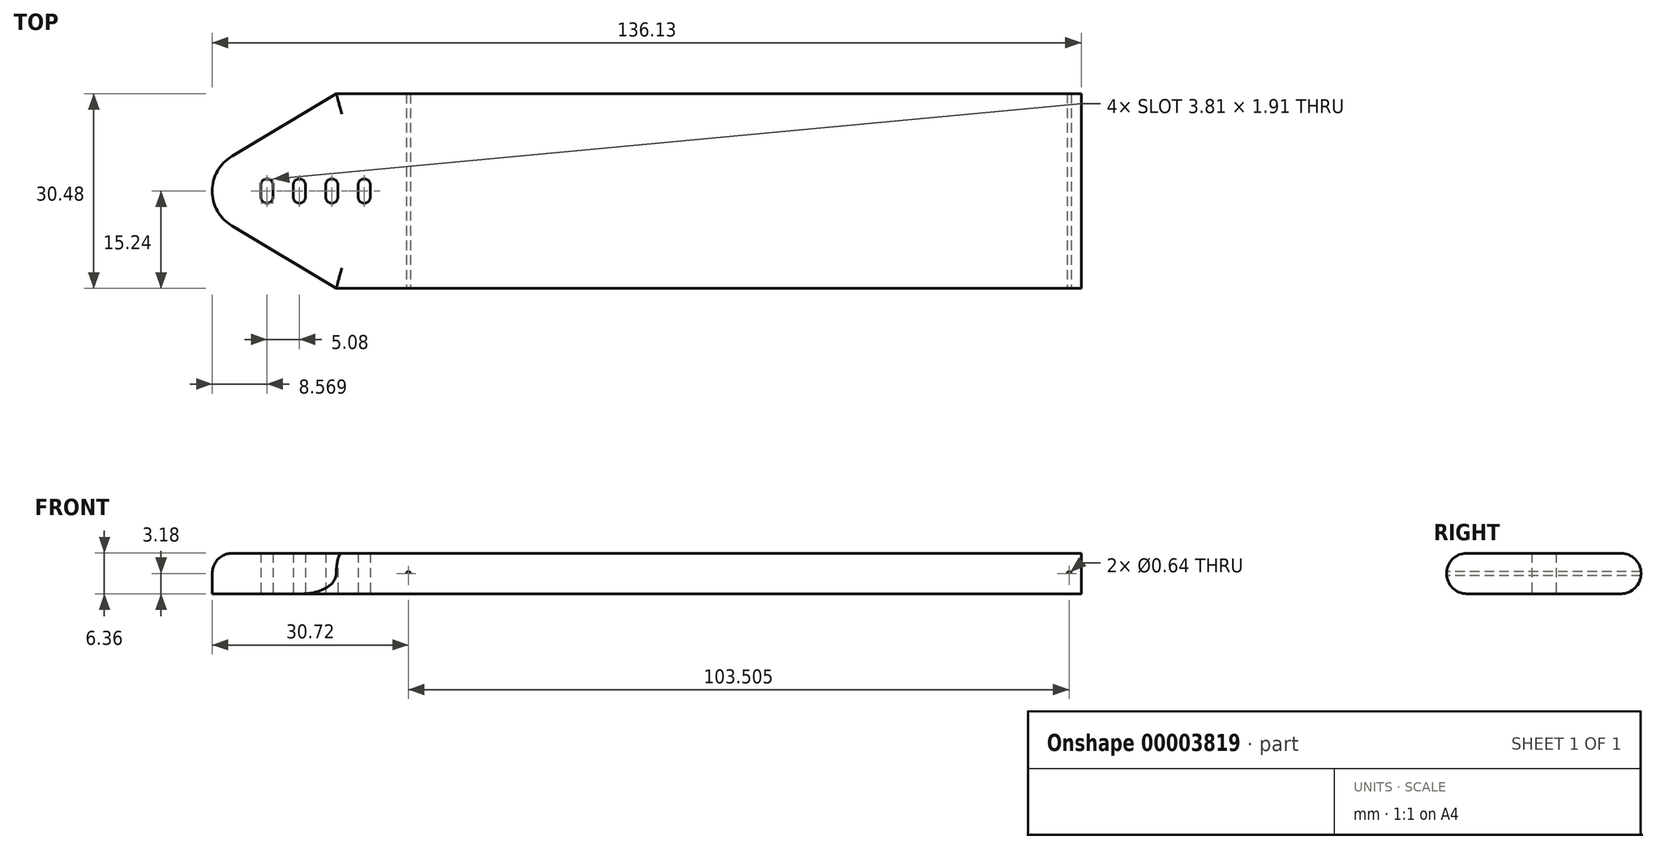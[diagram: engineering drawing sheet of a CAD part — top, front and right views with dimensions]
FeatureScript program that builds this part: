
annotation { "Feature Type Name" : "Feature", "Feature Type Description" : "" }
export const myFeature = defineFeature(function(context is Context, id is Id, definition is map)
    precondition{}
    {
        {
            var Q0;
            Q0=qCreatedBy(makeId("Right.planeOp"),FACE);
            var sketch = newSketch(context, id + "F0", { "sketchPlane" : qUnion([Q0])});
            skLineSegment(sketch, "E0.rect.bottom", {"start": v(15.24, -3.17) * mm, "end": v(-15.24, -3.18) * mm});
            skLineSegment(sketch, "E0.rect.top", {"start": v(15.24, 3.18) * mm, "end": v(-15.24, 3.18) * mm});
            skLineSegment(sketch, "E0.rect.left", {"start": v(15.24, -3.17) * mm, "end": v(15.24, 3.18) * mm});
            skLineSegment(sketch, "E0.rect.right", {"start": v(-15.24, -3.17) * mm, "end": v(-15.24, 3.18) * mm});
            skPoint(sketch, "E0.rect.middle", {"position": v(0, 0) * mm});
            skSolve(sketch);
        }
        {
            var Q0;
            Q0=qCreatedBy(makeId("Front.planeOp"),FACE);
            var sketch = newSketch(context, id + "F1", { "sketchPlane" : qUnion([Q0])});
            skLineSegment(sketch, "E1", {"start": v(0, 0) * mm, "end": v(95.25, 0) * mm});
            skPoint(sketch, "E2.end.orphan", {"position": v(0, 50.8) * mm});
            skSolve(sketch);
        }
        {
            var Q0;
            Q0=makeQuery(id+"F0.imprint","IMPRINT",FACE,{"disambiguationData":[TD([[makeQuery(id+"F0.imprint","IMPRINT",EDGE,{"derivedFrom":sQuery(id+"F0.wireOp",EDGE,"E0.rect.bottom")}),-1.0]])]});
            var Q1;
            Q1=sQuery(id+"F1.wireOp",EDGE,"E1");
            sweep(context, id + "F2", {"profiles" : qUnion([Q0]), "path" : qUnion([Q1])});
        }
        {
            var Q0;
            Q0=makeQuery(id+"F2.opSweep","CAP_FACE",FACE,{"disambiguationData":[OSD([sQuery(id+"F0.wireOp",EDGE,"E0.rect.bottom"),sQuery(id+"F0.wireOp",EDGE,"E0.rect.top"),sQuery(id+"F0.wireOp",EDGE,"E0.rect.left"),sQuery(id+"F0.wireOp",EDGE,"E0.rect.right"),sQuery(id+"F1.wireOp",VERTEX,"E1.end")])],"isStart":false});
            var sketch = newSketch(context, id + "F3", { "sketchPlane" : qUnion([Q0])});
            skLineSegment(sketch, "E3.bottom", {"start": v(15.24, 3.17) * mm, "end": v(-15.24, 3.17) * mm});
            skLineSegment(sketch, "E3.top", {"start": v(15.24, -3.17) * mm, "end": v(-15.24, -3.18) * mm});
            skLineSegment(sketch, "E3.left", {"start": v(-15.24, -3.18) * mm, "end": v(-15.24, 3.17) * mm});
            skLineSegment(sketch, "E3.right", {"start": v(15.24, -3.18) * mm, "end": v(15.24, 3.17) * mm});
            skSolve(sketch);
        }
        {
            var Q0;
            Q0=makeQuery(id+"F3.imprint","IMPRINT",FACE,{"disambiguationData":[TD([[makeQuery(id+"F3.imprint","IMPRINT",EDGE,{"derivedFrom":sQuery(id+"F3.wireOp",EDGE,"E3.bottom")}),1.0]])]});
            extrude(context, id + "F4", {"entities" : qUnion([Q0]), "operationType" : NewBodyOperationType.ADD, "depth" : 12.7 * mm});
        }
        {
            var Q0;
            Q0=makeQuery(id+"F4.boolean.opBoolean","MERGE",FACE,{"derivedFrom":[makeQuery(id+"F2.opSweep","SWEPT_FACE",FACE,{"disambiguationData":[OSD([sQuery(id+"F0.wireOp",EDGE,"E0.rect.right"),sQuery(id+"F1.wireOp",EDGE,"E1")])]}),makeQuery(id+"F4.opExtrude","SWEPT_FACE",FACE,{"disambiguationData":[OSD([sQuery(id+"F3.wireOp",EDGE,"E3.left")])]})]});
            var sketch = newSketch(context, id + "F5", { "sketchPlane" : qUnion([Q0])});
            skCircle(sketch, "E4", {"center": v(2.54, 0) * mm, "radius": 0.32 * mm});
            skSolve(sketch);
        }
        {
            var Q0;
            Q0=makeQuery(id+"F5.imprint","IMPRINT",FACE,{"disambiguationData":[TD([[makeQuery(id+"F5.imprint","IMPRINT",EDGE,{"derivedFrom":sQuery(id+"F5.wireOp",EDGE,"E4")}),1.0]])]});
            extrude(context, id + "F6", {"entities" : qUnion([Q0]), "operationType" : NewBodyOperationType.REMOVE, "endBound" : BoundingType.THROUGH_ALL, "oppositeDirection" : true, "depth" : 25.4 * mm});
        }
        {
            var Q0;
            Q0=makeQuery(id+"F4.boolean.opBoolean","MERGE",FACE,{"derivedFrom":[makeQuery(id+"F2.opSweep","SWEPT_FACE",FACE,{"disambiguationData":[OSD([sQuery(id+"F0.wireOp",EDGE,"E0.rect.right"),sQuery(id+"F1.wireOp",EDGE,"E1")])]}),makeQuery(id+"F4.opExtrude","SWEPT_FACE",FACE,{"disambiguationData":[OSD([sQuery(id+"F3.wireOp",EDGE,"E3.left")])]})]});
            var sketch = newSketch(context, id + "F7", { "sketchPlane" : qUnion([Q0])});
            skCircle(sketch, "E5", {"center": v(106.05, 0) * mm, "radius": 0.32 * mm});
            skLineSegment(sketch, "E6", {"start": v(107.95, 0) * mm, "end": v(114.08, 0) * mm, "construction": true});
            skSolve(sketch);
        }
        {
            var Q0;
            Q0=makeQuery(id+"F7.imprint","IMPRINT",FACE,{"disambiguationData":[TD([[makeQuery(id+"F7.imprint","IMPRINT",EDGE,{"derivedFrom":sQuery(id+"F7.wireOp",EDGE,"E5")}),1.0]])]});
            extrude(context, id + "F8", {"entities" : qUnion([Q0]), "operationType" : NewBodyOperationType.REMOVE, "endBound" : BoundingType.THROUGH_ALL, "oppositeDirection" : true, "depth" : 25.4 * mm});
        }
        {
            var Q0;
            Q0=makeQuery(id+"F2.opSweep","CAP_FACE",FACE,{"disambiguationData":[OSD([sQuery(id+"F0.wireOp",EDGE,"E0.rect.bottom"),sQuery(id+"F0.wireOp",EDGE,"E0.rect.top"),sQuery(id+"F0.wireOp",EDGE,"E0.rect.left"),sQuery(id+"F0.wireOp",EDGE,"E0.rect.right"),sQuery(id+"F1.wireOp",VERTEX,"E1.start")])],"isStart":true});
            var sketch = newSketch(context, id + "F9", { "sketchPlane" : qUnion([Q0])});
            skLineSegment(sketch, "E7.bottom", {"start": v(15.24, -3.18) * mm, "end": v(-15.24, -3.18) * mm});
            skLineSegment(sketch, "E7.top", {"start": v(15.24, 3.18) * mm, "end": v(-15.24, 3.18) * mm});
            skLineSegment(sketch, "E7.left", {"start": v(15.24, -3.18) * mm, "end": v(15.24, 3.18) * mm});
            skLineSegment(sketch, "E7.right", {"start": v(-15.24, -3.18) * mm, "end": v(-15.24, 3.18) * mm});
            skSolve(sketch);
        }
        {
            var Q0;
            Q0=makeQuery(id+"F9.imprint","IMPRINT",FACE,{"disambiguationData":[TD([[makeQuery(id+"F9.imprint","IMPRINT",EDGE,{"derivedFrom":sQuery(id+"F9.wireOp",EDGE,"E7.bottom")}),-1.0]])]});
            extrude(context, id + "F10", {"entities" : qUnion([Q0]), "operationType" : NewBodyOperationType.ADD, "depth" : 31.75 * mm});
        }
        {
            var Q0;
            Q0=makeQuery(id+"F10.boolean.opBoolean","MERGE",FACE,{"derivedFrom":[makeQuery(id+"F4.boolean.opBoolean","MERGE",FACE,{"derivedFrom":[makeQuery(id+"F2.opSweep","SWEPT_FACE",FACE,{"disambiguationData":[OSD([sQuery(id+"F0.wireOp",EDGE,"E0.rect.bottom"),sQuery(id+"F1.wireOp",EDGE,"E1")])]}),makeQuery(id+"F4.opExtrude","SWEPT_FACE",FACE,{"disambiguationData":[OSD([sQuery(id+"F3.wireOp",EDGE,"E3.top")])]})]}),makeQuery(id+"F10.opExtrude","SWEPT_FACE",FACE,{"disambiguationData":[OSD([sQuery(id+"F9.wireOp",EDGE,"E7.bottom")])]})]});
            var sketch = newSketch(context, id + "F11", { "sketchPlane" : qUnion([Q0])});
            skLineSegment(sketch, "E8", {"start": v(0, 0) * mm, "end": v(-31.75, 0) * mm, "construction": true});
            skLineSegment(sketch, "E9", {"start": v(-25.1, 5.45) * mm, "end": v(-8.76, 15.24) * mm});
            skLineSegment(sketch, "E10.0.MirrorCS", {"start": v(-25.1, -5.45) * mm, "end": v(-8.76, -15.24) * mm});
            skPoint(sketch, "E11.start.orphan", {"position": v(-34.19, 0) * mm});
            skArc(sketch, "E12.filletArc", {"start": v(-25.1, 5.45) * mm, "mid": v(-28.18, 0) * mm, "end": v(-25.1, -5.45) * mm});
            skLineSegment(sketch, "E13", {"start": v(-31.75, -15.24) * mm, "end": v(-31.75, 15.24) * mm});
            skLineSegment(sketch, "E14", {"start": v(-31.75, 15.24) * mm, "end": v(19.05, 15.24) * mm});
            skLineSegment(sketch, "E15", {"start": v(-8.76, 15.24) * mm, "end": v(-31.75, 15.24) * mm});
            skLineSegment(sketch, "E16", {"start": v(-31.75, 15.24) * mm, "end": v(-31.75, -15.24) * mm});
            skLineSegment(sketch, "E17", {"start": v(-31.75, -15.24) * mm, "end": v(-8.76, -15.24) * mm});
            skSolve(sketch);
        }
        {
            var Q0;
            Q0=makeQuery(id+"F11.imprint","IMPRINT",FACE,{"disambiguationData":[TD([[makeQuery(id+"F11.imprint","IMPRINT",EDGE,{"derivedFrom":sQuery(id+"F11.wireOp",EDGE,"E9")}),1.0]])]});
            extrude(context, id + "F12", {"entities" : qUnion([Q0]), "operationType" : NewBodyOperationType.REMOVE, "oppositeDirection" : true, "depth" : 25.4 * mm});
        }
        {
            var Q0;
            Q0=makeQuery(id+"F10.boolean.opBoolean","MERGE",FACE,{"derivedFrom":[makeQuery(id+"F4.boolean.opBoolean","MERGE",FACE,{"derivedFrom":[makeQuery(id+"F2.opSweep","SWEPT_FACE",FACE,{"disambiguationData":[OSD([sQuery(id+"F0.wireOp",EDGE,"E0.rect.bottom"),sQuery(id+"F1.wireOp",EDGE,"E1")])]}),makeQuery(id+"F4.opExtrude","SWEPT_FACE",FACE,{"disambiguationData":[OSD([sQuery(id+"F3.wireOp",EDGE,"E3.top")])]})]}),makeQuery(id+"F10.opExtrude","SWEPT_FACE",FACE,{"disambiguationData":[OSD([sQuery(id+"F9.wireOp",EDGE,"E7.bottom")])]})]});
            var sketch = newSketch(context, id + "F13", { "sketchPlane" : qUnion([Q0])});
            skLineSegment(sketch, "E18", {"start": v(-20.56, -0.95) * mm, "end": v(-20.56, 0.95) * mm});
            skLineSegment(sketch, "E19", {"start": v(-19.61, 1.9) * mm, "end": v(-19.61, 1.9) * mm});
            skLineSegment(sketch, "E20", {"start": v(-18.66, 0.95) * mm, "end": v(-18.66, -0.95) * mm});
            skLineSegment(sketch, "E21", {"start": v(-19.61, -1.9) * mm, "end": v(-19.61, -1.9) * mm});
            skPoint(sketch, "E22.visualSharp", {"position": v(-20.56, -1.9) * mm});
            skArc(sketch, "E22.filletArc", {"start": v(-20.56, -0.95) * mm, "mid": v(-20.28, -1.63) * mm, "end": v(-19.61, -1.9) * mm});
            skPoint(sketch, "E23.visualSharp", {"position": v(-18.66, -1.9) * mm});
            skArc(sketch, "E23.filletArc", {"start": v(-19.61, -1.9) * mm, "mid": v(-18.94, -1.63) * mm, "end": v(-18.66, -0.95) * mm});
            skPoint(sketch, "E24.visualSharp", {"position": v(-18.66, 1.9) * mm});
            skArc(sketch, "E24.filletArc", {"start": v(-18.66, 0.95) * mm, "mid": v(-18.94, 1.63) * mm, "end": v(-19.61, 1.9) * mm});
            skPoint(sketch, "E25.visualSharp", {"position": v(-20.56, 1.9) * mm});
            skArc(sketch, "E25.filletArc", {"start": v(-19.61, 1.9) * mm, "mid": v(-20.28, 1.63) * mm, "end": v(-20.56, 0.95) * mm});
            skPoint(sketch, "E26.1.0.0", {"position": v(-13.58, 1.9) * mm});
            skLineSegment(sketch, "E26.1.0.1", {"start": v(-13.58, 0.95) * mm, "end": v(-13.58, -0.95) * mm});
            skLineSegment(sketch, "E26.1.0.2", {"start": v(-15.48, -0.95) * mm, "end": v(-15.48, 0.95) * mm});
            skArc(sketch, "E26.1.0.3", {"start": v(-13.58, 0.95) * mm, "mid": v(-13.86, 1.63) * mm, "end": v(-14.53, 1.9) * mm});
            skArc(sketch, "E26.1.0.4", {"start": v(-14.53, 1.9) * mm, "mid": v(-15.2, 1.63) * mm, "end": v(-15.48, 0.95) * mm});
            skArc(sketch, "E26.1.0.5", {"start": v(-14.53, -1.9) * mm, "mid": v(-13.86, -1.63) * mm, "end": v(-13.58, -0.95) * mm});
            skArc(sketch, "E26.1.0.6", {"start": v(-15.48, -0.95) * mm, "mid": v(-15.2, -1.63) * mm, "end": v(-14.53, -1.9) * mm});
            skPoint(sketch, "E26.1.0.7", {"position": v(-15.48, 1.9) * mm});
            skPoint(sketch, "E26.1.0.8", {"position": v(-13.58, -1.9) * mm});
            skPoint(sketch, "E26.1.0.9", {"position": v(-15.48, -1.9) * mm});
            skPoint(sketch, "E26.2.0.0", {"position": v(-8.5, 1.9) * mm});
            skLineSegment(sketch, "E26.2.0.1", {"start": v(-8.5, 0.95) * mm, "end": v(-8.5, -0.95) * mm});
            skLineSegment(sketch, "E26.2.0.2", {"start": v(-10.4, -0.95) * mm, "end": v(-10.4, 0.95) * mm});
            skArc(sketch, "E26.2.0.3", {"start": v(-8.5, 0.95) * mm, "mid": v(-8.78, 1.63) * mm, "end": v(-9.45, 1.9) * mm});
            skArc(sketch, "E26.2.0.4", {"start": v(-9.45, 1.9) * mm, "mid": v(-10.12, 1.63) * mm, "end": v(-10.4, 0.95) * mm});
            skArc(sketch, "E26.2.0.5", {"start": v(-9.45, -1.9) * mm, "mid": v(-8.78, -1.63) * mm, "end": v(-8.5, -0.95) * mm});
            skArc(sketch, "E26.2.0.6", {"start": v(-10.4, -0.95) * mm, "mid": v(-10.12, -1.63) * mm, "end": v(-9.45, -1.9) * mm});
            skPoint(sketch, "E26.2.0.7", {"position": v(-10.4, 1.9) * mm});
            skPoint(sketch, "E26.2.0.8", {"position": v(-8.5, -1.9) * mm});
            skPoint(sketch, "E26.2.0.9", {"position": v(-10.4, -1.9) * mm});
            skPoint(sketch, "E26.3.0.0", {"position": v(-3.42, 1.9) * mm});
            skLineSegment(sketch, "E26.3.0.1", {"start": v(-3.42, 0.95) * mm, "end": v(-3.42, -0.95) * mm});
            skLineSegment(sketch, "E26.3.0.2", {"start": v(-5.32, -0.95) * mm, "end": v(-5.32, 0.95) * mm});
            skArc(sketch, "E26.3.0.3", {"start": v(-3.42, 0.95) * mm, "mid": v(-3.7, 1.63) * mm, "end": v(-4.37, 1.9) * mm});
            skArc(sketch, "E26.3.0.4", {"start": v(-4.37, 1.9) * mm, "mid": v(-5.04, 1.63) * mm, "end": v(-5.32, 0.95) * mm});
            skArc(sketch, "E26.3.0.5", {"start": v(-4.37, -1.9) * mm, "mid": v(-3.7, -1.63) * mm, "end": v(-3.42, -0.95) * mm});
            skArc(sketch, "E26.3.0.6", {"start": v(-5.32, -0.95) * mm, "mid": v(-5.04, -1.63) * mm, "end": v(-4.37, -1.9) * mm});
            skPoint(sketch, "E26.3.0.7", {"position": v(-5.32, 1.9) * mm});
            skPoint(sketch, "E26.3.0.8", {"position": v(-3.42, -1.9) * mm});
            skPoint(sketch, "E26.3.0.9", {"position": v(-5.32, -1.9) * mm});
            skLineSegment(sketch, "E26.direction1", {"start": v(-18.66, 1.9) * mm, "end": v(-13.58, 1.9) * mm, "construction": true});
            skSolve(sketch);
        }
        {
            var Q0;
            {Q0=qUnion([makeQuery(id+"F13.imprint","IMPRINT",FACE,{"disambiguationData":[TD([[makeQuery(id+"F13.imprint","IMPRINT",EDGE,{"derivedFrom":sQuery(id+"F13.wireOp",EDGE,"E18")}),-1.0]])]}),makeQuery(id+"F13.imprint","IMPRINT",FACE,{"disambiguationData":[TD([[makeQuery(id+"F13.imprint","IMPRINT",EDGE,{"derivedFrom":sQuery(id+"F13.wireOp",EDGE,"E26.1.0.1")}),-1.0]])]}),makeQuery(id+"F13.imprint","IMPRINT",FACE,{"disambiguationData":[TD([[makeQuery(id+"F13.imprint","IMPRINT",EDGE,{"derivedFrom":sQuery(id+"F13.wireOp",EDGE,"E26.2.0.1")}),-1.0]])]}),makeQuery(id+"F13.imprint","IMPRINT",FACE,{"disambiguationData":[TD([[makeQuery(id+"F13.imprint","IMPRINT",EDGE,{"derivedFrom":sQuery(id+"F13.wireOp",EDGE,"E26.3.0.1")}),-1.0]])]})]);}
            extrude(context, id + "F14", {"entities" : qUnion([Q0]), "operationType" : NewBodyOperationType.REMOVE, "oppositeDirection" : true, "depth" : 6.35 * mm});
        }
        {
            var Q0;
            Q0=makeQuery(id+"F10.boolean.opBoolean","MERGE",EDGE,{"derivedFrom":[makeQuery(id+"F4.boolean.opBoolean","MERGE",EDGE,{"derivedFrom":[makeQuery(id+"F2.opSweep","SWEPT_EDGE",EDGE,{"disambiguationData":[OSD([sQuery(id+"F0.wireOp",EDGE,"E0.rect.bottom"),sQuery(id+"F0.wireOp",EDGE,"E0.rect.right"),sQuery(id+"F1.wireOp",EDGE,"E1")])]}),makeQuery(id+"F4.opExtrude","SWEPT_EDGE",EDGE,{"disambiguationData":[OSD([sQuery(id+"F3.wireOp",EDGE,"E3.top"),sQuery(id+"F3.wireOp",EDGE,"E3.left")])]})]}),makeQuery(id+"F10.opExtrude","SWEPT_EDGE",EDGE,{"disambiguationData":[OSD([sQuery(id+"F9.wireOp",EDGE,"E7.bottom"),sQuery(id+"F9.wireOp",EDGE,"E7.left")])]})]});
            var Q1;
            Q1=makeQuery(id+"F12.boolean.opBoolean","COPY",EDGE,{"derivedFrom":makeQuery(id+"F12.opExtrude","CAP_EDGE",EDGE,{"disambiguationData":[OSD([sQuery(id+"F11.wireOp",EDGE,"E9")])],"isStart":true})});
            var Q2;
            Q2=makeQuery(id+"F12.boolean.opBoolean","COPY",EDGE,{"derivedFrom":makeQuery(id+"F12.opExtrude","CAP_EDGE",EDGE,{"disambiguationData":[OSD([sQuery(id+"F11.wireOp",EDGE,"E12.filletArc")])],"isStart":true})});
            var Q3;
            Q3=makeQuery(id+"F12.boolean.opBoolean","COPY",EDGE,{"derivedFrom":makeQuery(id+"F12.opExtrude","CAP_EDGE",EDGE,{"disambiguationData":[OSD([sQuery(id+"F11.wireOp",EDGE,"E10.0.MirrorCS")])],"isStart":true})});
            var Q4;
            Q4=makeQuery(id+"F10.boolean.opBoolean","MERGE",EDGE,{"derivedFrom":[makeQuery(id+"F4.boolean.opBoolean","MERGE",EDGE,{"derivedFrom":[makeQuery(id+"F2.opSweep","SWEPT_EDGE",EDGE,{"disambiguationData":[OSD([sQuery(id+"F0.wireOp",EDGE,"E0.rect.bottom"),sQuery(id+"F0.wireOp",EDGE,"E0.rect.left"),sQuery(id+"F1.wireOp",EDGE,"E1")])]}),makeQuery(id+"F4.opExtrude","SWEPT_EDGE",EDGE,{"disambiguationData":[OSD([sQuery(id+"F3.wireOp",EDGE,"E3.top"),sQuery(id+"F3.wireOp",EDGE,"E3.right")])]})]}),makeQuery(id+"F10.opExtrude","SWEPT_EDGE",EDGE,{"disambiguationData":[OSD([sQuery(id+"F9.wireOp",EDGE,"E7.bottom"),sQuery(id+"F9.wireOp",EDGE,"E7.right")])]})]});
            var Q5;
            Q5=makeQuery(id+"F12.boolean.opBoolean","INTERSECT",EDGE,{"derivedFrom":[makeQuery(id+"F10.boolean.opBoolean","MERGE",FACE,{"derivedFrom":[makeQuery(id+"F4.boolean.opBoolean","MERGE",FACE,{"derivedFrom":[makeQuery(id+"F2.opSweep","SWEPT_FACE",FACE,{"disambiguationData":[OSD([sQuery(id+"F0.wireOp",EDGE,"E0.rect.top"),sQuery(id+"F1.wireOp",EDGE,"E1")])]}),makeQuery(id+"F4.opExtrude","SWEPT_FACE",FACE,{"disambiguationData":[OSD([sQuery(id+"F3.wireOp",EDGE,"E3.bottom")])]})]}),makeQuery(id+"F10.opExtrude","SWEPT_FACE",FACE,{"disambiguationData":[OSD([sQuery(id+"F9.wireOp",EDGE,"E7.top")])]})]}),makeQuery(id+"F12.opExtrude","SWEPT_FACE",FACE,{"disambiguationData":[OSD([sQuery(id+"F11.wireOp",EDGE,"E9")])]})]});
            var Q6;
            Q6=makeQuery(id+"F10.boolean.opBoolean","MERGE",EDGE,{"derivedFrom":[makeQuery(id+"F4.boolean.opBoolean","MERGE",EDGE,{"derivedFrom":[makeQuery(id+"F2.opSweep","SWEPT_EDGE",EDGE,{"disambiguationData":[OSD([sQuery(id+"F0.wireOp",EDGE,"E0.rect.top"),sQuery(id+"F0.wireOp",EDGE,"E0.rect.right"),sQuery(id+"F1.wireOp",EDGE,"E1")])]}),makeQuery(id+"F4.opExtrude","SWEPT_EDGE",EDGE,{"disambiguationData":[OSD([sQuery(id+"F3.wireOp",EDGE,"E3.bottom"),sQuery(id+"F3.wireOp",EDGE,"E3.left")])]})]}),makeQuery(id+"F10.opExtrude","SWEPT_EDGE",EDGE,{"disambiguationData":[OSD([sQuery(id+"F9.wireOp",EDGE,"E7.top"),sQuery(id+"F9.wireOp",EDGE,"E7.left")])]})]});
            var Q7;
            Q7=makeQuery(id+"F12.boolean.opBoolean","INTERSECT",EDGE,{"derivedFrom":[makeQuery(id+"F10.boolean.opBoolean","MERGE",FACE,{"derivedFrom":[makeQuery(id+"F4.boolean.opBoolean","MERGE",FACE,{"derivedFrom":[makeQuery(id+"F2.opSweep","SWEPT_FACE",FACE,{"disambiguationData":[OSD([sQuery(id+"F0.wireOp",EDGE,"E0.rect.top"),sQuery(id+"F1.wireOp",EDGE,"E1")])]}),makeQuery(id+"F4.opExtrude","SWEPT_FACE",FACE,{"disambiguationData":[OSD([sQuery(id+"F3.wireOp",EDGE,"E3.bottom")])]})]}),makeQuery(id+"F10.opExtrude","SWEPT_FACE",FACE,{"disambiguationData":[OSD([sQuery(id+"F9.wireOp",EDGE,"E7.top")])]})]}),makeQuery(id+"F12.opExtrude","SWEPT_FACE",FACE,{"disambiguationData":[OSD([sQuery(id+"F11.wireOp",EDGE,"E12.filletArc")])]})]});
            var Q8;
            Q8=makeQuery(id+"F12.boolean.opBoolean","INTERSECT",EDGE,{"derivedFrom":[makeQuery(id+"F10.boolean.opBoolean","MERGE",FACE,{"derivedFrom":[makeQuery(id+"F4.boolean.opBoolean","MERGE",FACE,{"derivedFrom":[makeQuery(id+"F2.opSweep","SWEPT_FACE",FACE,{"disambiguationData":[OSD([sQuery(id+"F0.wireOp",EDGE,"E0.rect.top"),sQuery(id+"F1.wireOp",EDGE,"E1")])]}),makeQuery(id+"F4.opExtrude","SWEPT_FACE",FACE,{"disambiguationData":[OSD([sQuery(id+"F3.wireOp",EDGE,"E3.bottom")])]})]}),makeQuery(id+"F10.opExtrude","SWEPT_FACE",FACE,{"disambiguationData":[OSD([sQuery(id+"F9.wireOp",EDGE,"E7.top")])]})]}),makeQuery(id+"F12.opExtrude","SWEPT_FACE",FACE,{"disambiguationData":[OSD([sQuery(id+"F11.wireOp",EDGE,"E10.0.MirrorCS")])]})]});
            var Q9;
            Q9=makeQuery(id+"F10.boolean.opBoolean","MERGE",EDGE,{"derivedFrom":[makeQuery(id+"F4.boolean.opBoolean","MERGE",EDGE,{"derivedFrom":[makeQuery(id+"F2.opSweep","SWEPT_EDGE",EDGE,{"disambiguationData":[OSD([sQuery(id+"F0.wireOp",EDGE,"E0.rect.top"),sQuery(id+"F0.wireOp",EDGE,"E0.rect.left"),sQuery(id+"F1.wireOp",EDGE,"E1")])]}),makeQuery(id+"F4.opExtrude","SWEPT_EDGE",EDGE,{"disambiguationData":[OSD([sQuery(id+"F3.wireOp",EDGE,"E3.bottom"),sQuery(id+"F3.wireOp",EDGE,"E3.right")])]})]}),makeQuery(id+"F10.opExtrude","SWEPT_EDGE",EDGE,{"disambiguationData":[OSD([sQuery(id+"F9.wireOp",EDGE,"E7.top"),sQuery(id+"F9.wireOp",EDGE,"E7.right")])]})]});
            fillet(context, id + "F15", {"entities" : qUnion([Q0, Q1, Q2, Q3, Q4, Q5, Q6, Q7, Q8, Q9]), "radius" : 3.17 * mm, "tangentPropagation" : true, "allowEdgeOverflow" : false});
        }
    });
